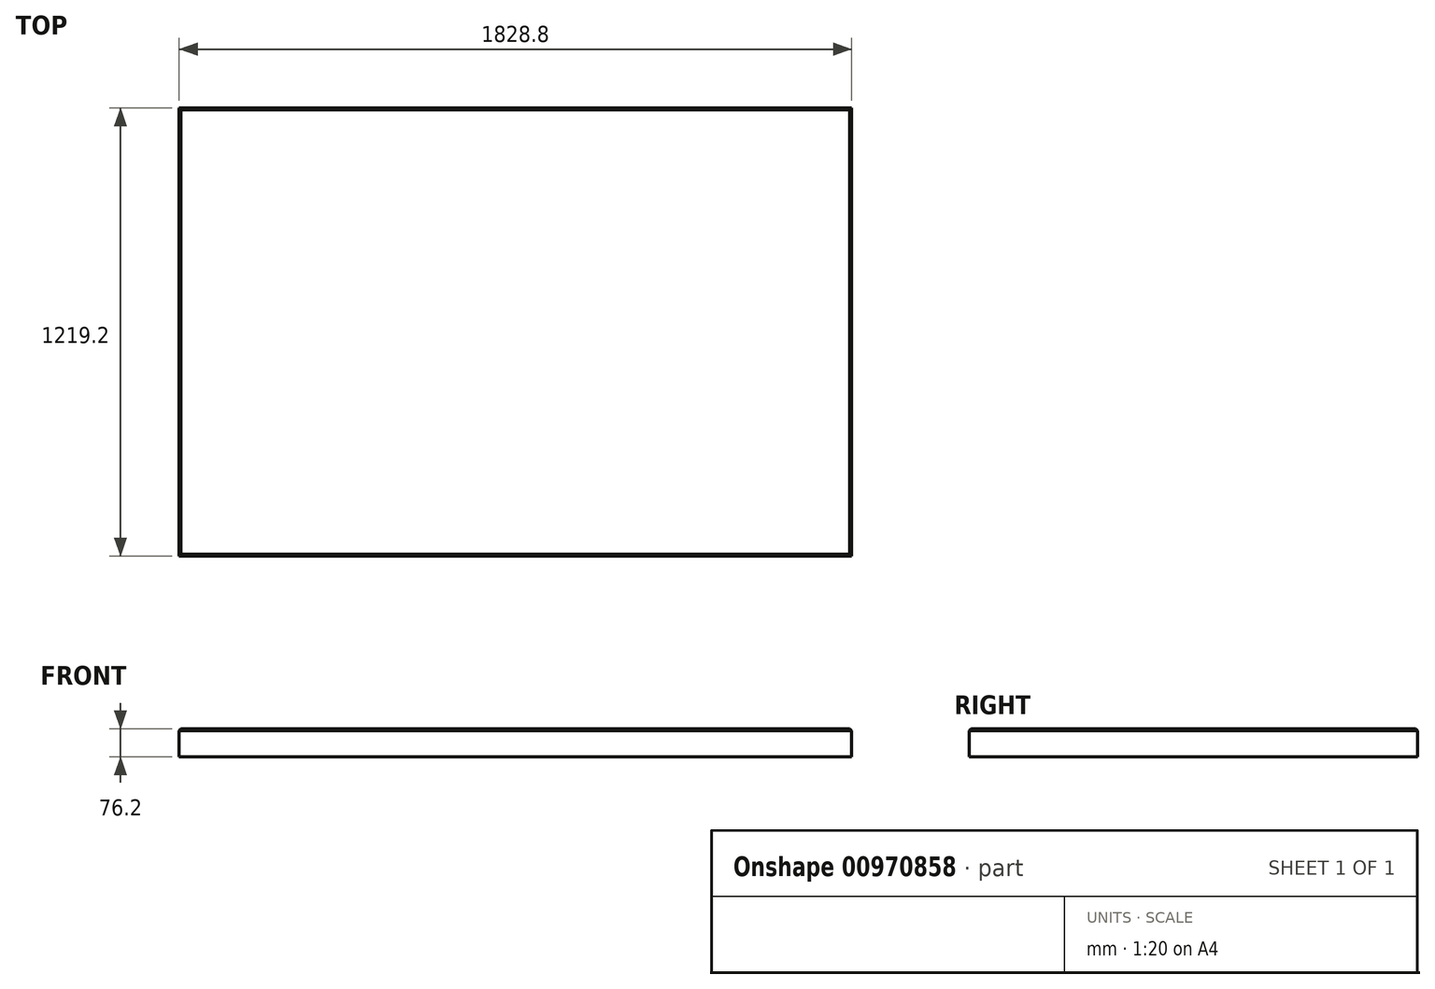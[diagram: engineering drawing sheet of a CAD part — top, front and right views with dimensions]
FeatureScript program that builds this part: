
annotation { "Feature Type Name" : "Feature", "Feature Type Description" : "" }
export const myFeature = defineFeature(function(context is Context, id is Id, definition is map)
    precondition{}
    {
        {
            var Q0;
            Q0=qCreatedBy(makeId("Top.planeOp"),FACE);
            var sketch = newSketch(context, id + "F0", { "sketchPlane" : qUnion([Q0])});
            skLineSegment(sketch, "E0.bottom", {"start": v(0, 0) * mm, "end": v(-1828.8, 0) * mm});
            skLineSegment(sketch, "E0.top", {"start": v(0, 1219.2) * mm, "end": v(-1828.8, 1219.2) * mm});
            skLineSegment(sketch, "E0.left", {"start": v(0, 0) * mm, "end": v(0, 1219.2) * mm});
            skLineSegment(sketch, "E0.right", {"start": v(-1828.8, 0) * mm, "end": v(-1828.8, 1219.2) * mm});
            skSolve(sketch);
        }
        {
            var Q0;
            Q0=makeQuery(id+"F0.imprint","IMPRINT",FACE,{"disambiguationData":[TD([[makeQuery(id+"F0.imprint","IMPRINT",EDGE,{"derivedFrom":sQuery(id+"F0.wireOp",EDGE,"E0.bottom")}),-1.0]])]});
            extrude(context, id + "F1", {"entities" : qUnion([Q0]), "depth" : 76.2 * mm, "offsetDistance" : 25.4 * mm});
        }
        {
            var Q0;
            Q0=makeQuery(id+"F1.opExtrude","CAP_EDGE",EDGE,{"disambiguationData":[OSD([sQuery(id+"F0.wireOp",EDGE,"E0.bottom")])],"isStart":false});
            var Q1;
            Q1=makeQuery(id+"F1.opExtrude","CAP_EDGE",EDGE,{"disambiguationData":[OSD([sQuery(id+"F0.wireOp",EDGE,"E0.left")])],"isStart":false});
            var Q2;
            Q2=makeQuery(id+"F1.opExtrude","CAP_EDGE",EDGE,{"disambiguationData":[OSD([sQuery(id+"F0.wireOp",EDGE,"E0.top")])],"isStart":false});
            var Q3;
            Q3=makeQuery(id+"F1.opExtrude","CAP_EDGE",EDGE,{"disambiguationData":[OSD([sQuery(id+"F0.wireOp",EDGE,"E0.right")])],"isStart":false});
            chamfer(context, id + "F2", {"entities" : qUnion([Q0, Q1, Q2, Q3]), "width" : 5.08 * mm, "tangentPropagation" : true});
        }
    });
